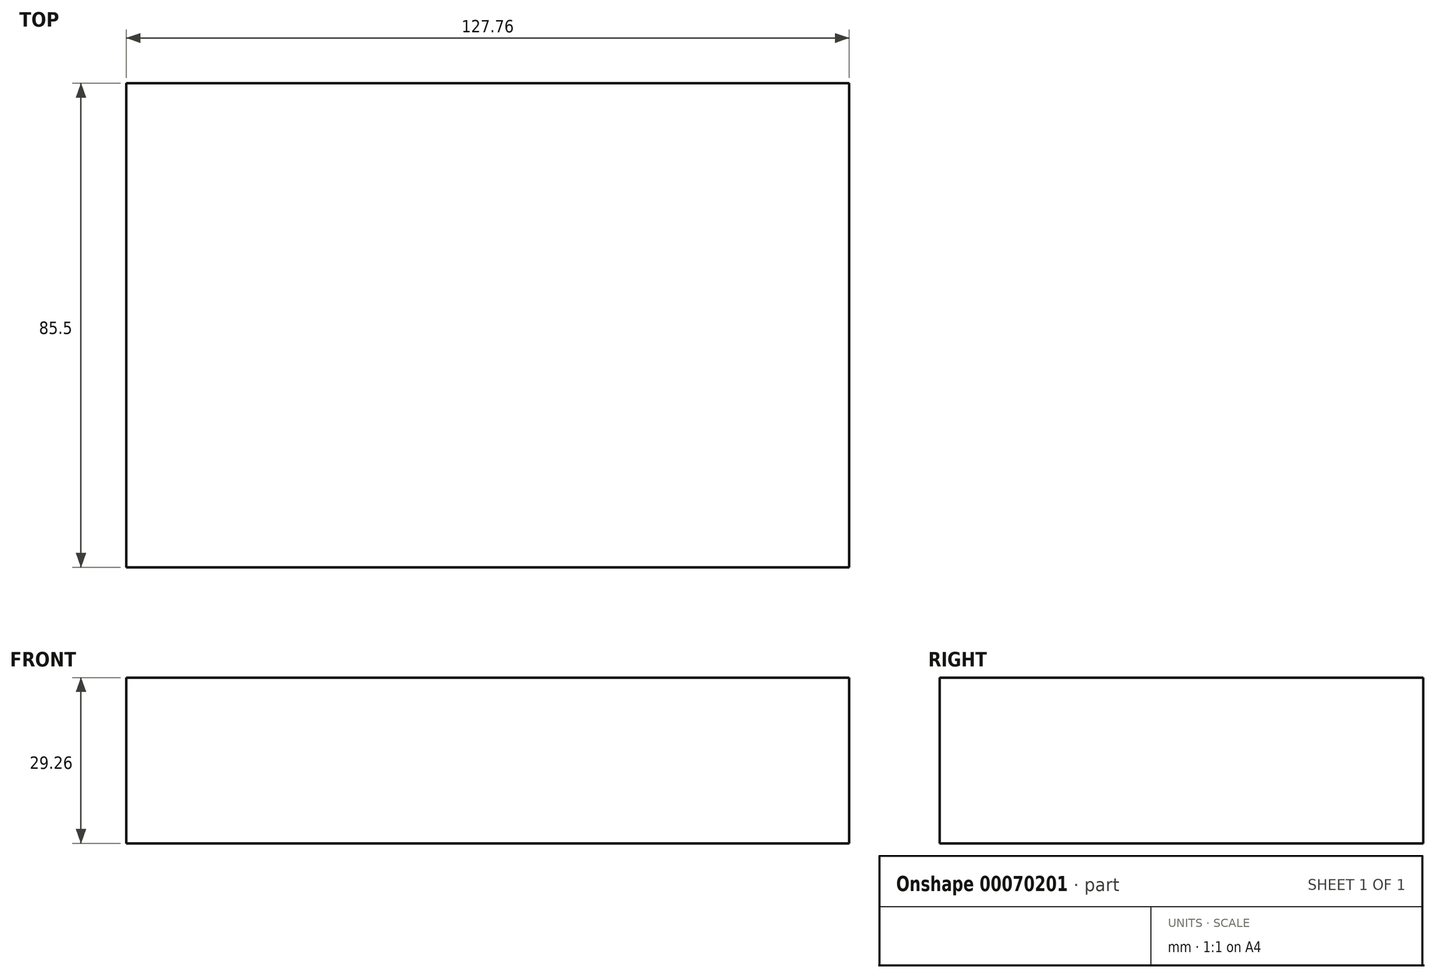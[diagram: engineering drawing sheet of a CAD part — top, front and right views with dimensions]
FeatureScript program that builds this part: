
annotation { "Feature Type Name" : "Feature", "Feature Type Description" : "" }
export const myFeature = defineFeature(function(context is Context, id is Id, definition is map)
    precondition{}
    {
        {
            var Q0;
            Q0=qCreatedBy(makeId("Top.planeOp"),FACE);
            var sketch = newSketch(context, id + "F0", { "sketchPlane" : qUnion([Q0])});
            skLineSegment(sketch, "E0.rect.bottom", {"start": v(63.88, 42.75) * mm, "end": v(-63.88, 42.75) * mm});
            skLineSegment(sketch, "E0.rect.top", {"start": v(63.88, -42.75) * mm, "end": v(-63.88, -42.75) * mm});
            skLineSegment(sketch, "E0.rect.left", {"start": v(63.88, 42.75) * mm, "end": v(63.88, -42.75) * mm});
            skLineSegment(sketch, "E0.rect.right", {"start": v(-63.88, 42.75) * mm, "end": v(-63.88, -42.75) * mm});
            skPoint(sketch, "E0.rect.middle", {"position": v(0, 0) * mm});
            skSolve(sketch);
        }
        {
            assignVariable(context, id + "F1", {"name" : "heigth", "anyValue" : 29.26});
        }
        {
            var Q0;
            Q0=makeQuery(id+"F0.imprint","IMPRINT",FACE,{"disambiguationData":[TD([[makeQuery(id+"F0.imprint","IMPRINT",EDGE,{"derivedFrom":sQuery(id+"F0.wireOp",EDGE,"E0.rect.bottom")}),1.0]])]});
            extrude(context, id + "F2", {"entities" : qUnion([Q0]), "depth" : (getVariable(context, 'heigth')) * mm});
        }
    });
